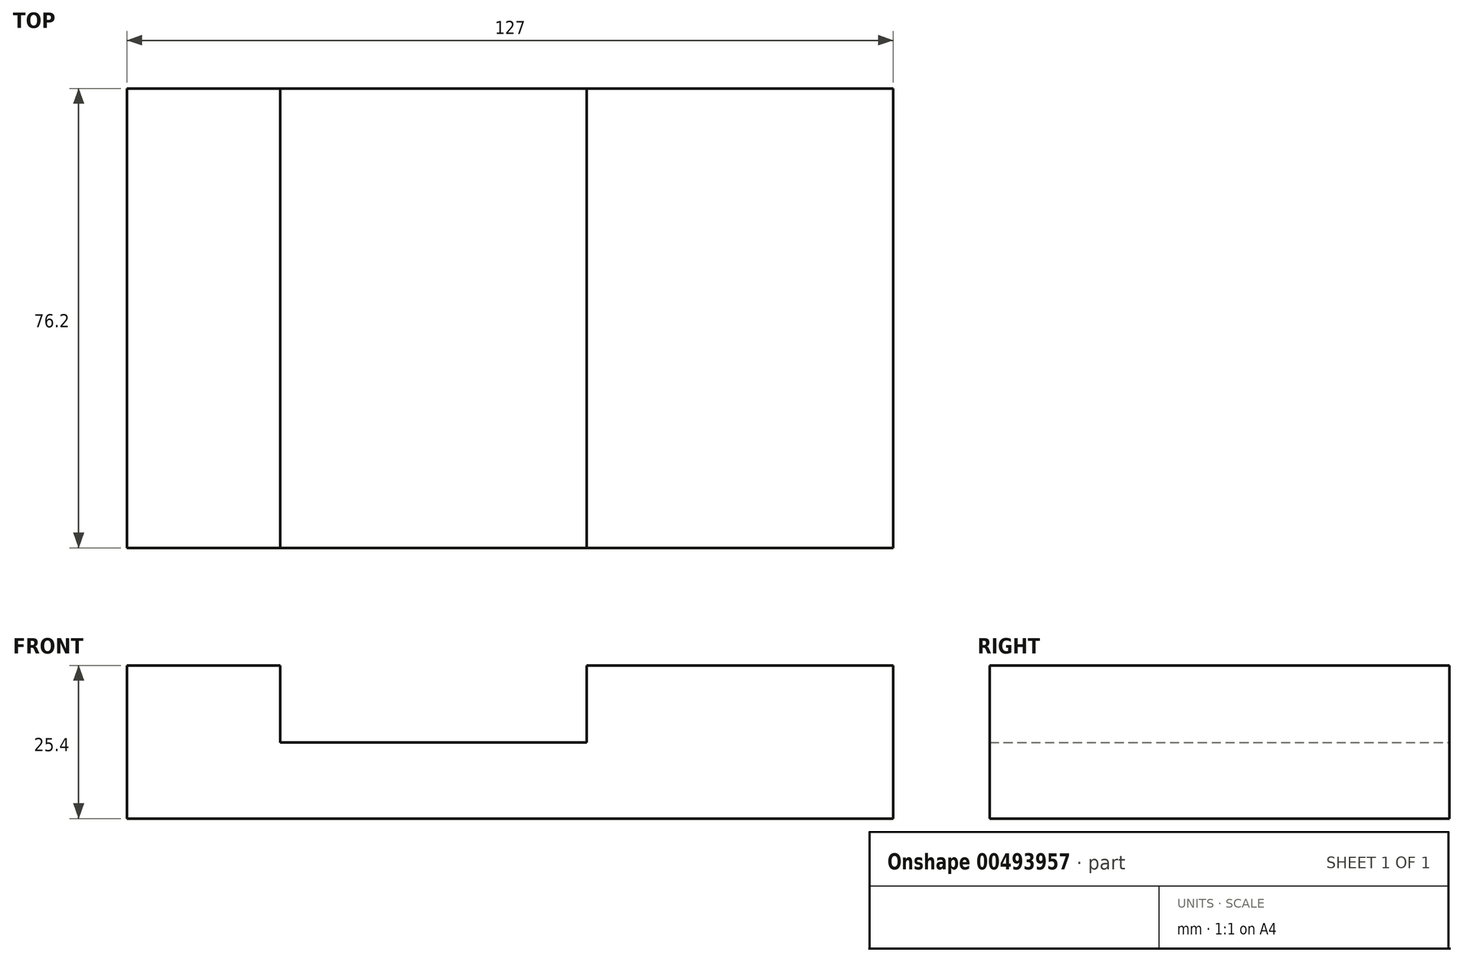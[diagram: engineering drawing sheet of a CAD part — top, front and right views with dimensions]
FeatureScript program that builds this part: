
annotation { "Feature Type Name" : "Feature", "Feature Type Description" : "" }
export const myFeature = defineFeature(function(context is Context, id is Id, definition is map)
    precondition{}
    {
        {
            var Q0;
            Q0=qCreatedBy(makeId("Front.planeOp"),FACE);
            var sketch = newSketch(context, id + "F0", { "sketchPlane" : qUnion([Q0])});
            skLineSegment(sketch, "E0.bottom", {"start": v(50.8, 12.8) * mm, "end": v(0, 12.8) * mm});
            skLineSegment(sketch, "E0.top", {"start": v(50.8, -12.6) * mm, "end": v(0, -12.6) * mm});
            skLineSegment(sketch, "E0.left", {"start": v(50.8, 12.8) * mm, "end": v(50.8, -12.6) * mm});
            skLineSegment(sketch, "E0.right", {"start": v(0, 12.8) * mm, "end": v(0, 0) * mm});
            skLineSegment(sketch, "E1.bottom", {"start": v(0, -12.6) * mm, "end": v(-76.2, -12.6) * mm});
            skLineSegment(sketch, "E1.top", {"start": v(0, 0) * mm, "end": v(-50.8, 0) * mm});
            skLineSegment(sketch, "E1.right", {"start": v(-76.2, -12.6) * mm, "end": v(-76.2, 0) * mm});
            skLineSegment(sketch, "E2.bottom", {"start": v(-76.2, -12.6) * mm, "end": v(-50.8, -12.6) * mm});
            skLineSegment(sketch, "E2.top", {"start": v(-76.2, 12.8) * mm, "end": v(-50.8, 12.8) * mm});
            skLineSegment(sketch, "E2.left", {"start": v(-76.2, -12.6) * mm, "end": v(-76.2, 12.8) * mm});
            skLineSegment(sketch, "E2.right", {"start": v(-50.8, 0) * mm, "end": v(-50.8, 12.8) * mm});
            skSolve(sketch);
        }
        {
            var Q0;
            Q0=makeQuery(id+"F0.imprint","IMPRINT",FACE,{"disambiguationData":[TD([[makeQuery(id+"F0.imprint","IMPRINT",EDGE,{"derivedFrom":sQuery(id+"F0.wireOp",EDGE,"E0.bottom")}),1.0]])]});
            extrude(context, id + "F1", {"entities" : qUnion([Q0]), "depth" : 76.2 * mm});
        }
    });
